# Revit family: LAMP_FIL 70 OPAL SUSPENDED DALI
name_source: partatom
category: Luminarias
revit_build: Autodesk Revit 2015 (Build: 20140606_1530(x64)
units: mm (PartAtom-declared; Revit-internal decimal feet)

## types (16) — shared parameters
CRI = 80
Cambio de temperatura de color de luz atenuada = <Ninguno>
Comentarios de tipo = Availability of switching between accessories through visibility parameters when placed in a project.
Fabricante = LAMP
Filtro de color = 16777215
Gear = Adjustable DALI
IEE = A+
IFC Clasificación = Light Fixture
Installation instructions = https://www.lamp.es
Insulation class = I
Last update = 12/08/2020
Luminaire type = Indoor - Modular System
Lámpara = LED MID-POWER
MacAdam = 3
Manufacturer URL = http://www.lamp.es
Manufacturer country = Spain
Manufacturer name = LAMP
Material Difusor = LAMP_PC Difusor Opal Fil
Model explanation = Availability of switching between accessories through visibility parameters when placed in a project.
Power Supply = 220-240V 50-60Hz
Product URL = https://www.lamp.es
Product datasheet = https://www.lamp.es
Protection rating = IP42, IK06
Type = MID POWER PHILIPS
Ángulo de inclinación = 90,00°

## per-type parameters (varying)
| type | Archivo de red fotométrica | Descripción | Dimensiones | Efficacy | Finish | LED Lifetime | Largo | Longitud de línea de emisión | Material Perfil | Material codo | Modelo | Plum | Power | Product code | UniClass 1.4 Code | UniClass 2.0 Code | Weight |
| 1162MM 2600LM 3000K GREY | 4741483.IES | FIL 70 OPAL SUS 2600 WW DALI GR. | 1.162x70x70mm | 104 lm/W | Gloss Grey | 60000 L80 B10 | 1162 mm  [stored 3.81234 ft] | 1162 mm  [stored 3.81234 ft] | LAMP_Aluminio Perfil Fil GR | LAMP_Aluminio Perfil Fil GR | F71SF120LOOP830DG | 19 W | 17 W | F71SF120LOOP830DG | F71SF120LOOP830DG | F71SF120LOOP830DG | 2,54 kg |
| 1162MM 2600LM 3000K WHITE | 4741480.IES | FIL 70 OPAL SUS 2600 WW DALI WH. | 1.162x70x70mm | 104 lm/W | Matt White | 60000 L80 B10 | 1162 mm  [stored 3.81234 ft] | 1162 mm  [stored 3.81234 ft] | LAMP_Aluminio Perfil Fil BL | LAMP_Aluminio Perfil Fil BL | F71SF120LOOP830DW | 19 W | 17 W | F71SF120LOOP830DW | F71SF120LOOP830DW | F71SF120LOOP830DW | 2,54 kg |
| 1162MM 2600LM 4000K GREY | 4740483.IES | FIL 70 OPAL SUS 2600 NW DALI GR. | 1.162x70x70mm | 112 lm/W | Gloss Grey | 60000 L80 B10 | 1162 mm  [stored 3.81234 ft] | 1162 mm  [stored 3.81234 ft] | LAMP_Aluminio Perfil Fil GR | LAMP_Aluminio Perfil Fil GR | F71SF120LOOP840DG | 19 W | 17 W | F71SF120LOOP840DG | F71SF120LOOP840DG | F71SF120LOOP840DG | 2,54 kg |
| 1162MM 2600LM 4000K WHITE | 4740480.IES | FIL 70 OPAL SUS 2600 NW DALI WH. | 1.162x70x70mm | 112 lm/W | Matt White | 60000 L80 B10 | 1162 mm  [stored 3.81234 ft] | 1162 mm  [stored 3.81234 ft] | LAMP_Aluminio Perfil Fil BL | LAMP_Aluminio Perfil Fil BL | F71SF120LOOP840DW | 19 W | 17 W | F71SF120LOOP840DW | F71SF120LOOP840DW | F71SF120LOOP840DW | 2,54 kg |
| 1162MM 4400LM 3000K GREY | 4741563.IES | FIL 70 OPAL SUS 4400 WW DALI GR. | 1.162x70x70mm | 110 lm/W | Gloss Grey | 60000 L80 B10 | 1162 mm  [stored 3.81234 ft] | 1162 mm  [stored 3.81234 ft] | LAMP_Aluminio Perfil Fil GR | LAMP_Aluminio Perfil Fil GR | F71SF120HOOP830DG | 31 W | 28 W | F71SF120HOOP830DG | F71SF120HOOP830DG | F71SF120HOOP830DG | 2,53 kg |
| 1162MM 4400LM 3000K WHITE | 4741560.IES | FIL 70 OPAL SUS 4400 WW DALI WH. | 1.162x70x70mm | 110 lm/W | Matt White | 60000 L80 B10 | 1162 mm  [stored 3.81234 ft] | 1162 mm  [stored 3.81234 ft] | LAMP_Aluminio Perfil Fil BL | LAMP_Aluminio Perfil Fil BL | F71SF120HOOP830DW | 31 W | 28 W | F71SF120HOOP830DW | F71SF120HOOP830DW | F71SF120HOOP830DW | 2,53 kg |
| 1162MM 4400LM 4000K GREY | 4740563.IES | FIL 70 OPAL SUS 4400 NW DALI GR. | 1.162x70x70mm | 116 lm/W | Gloss Grey | 60000 L80 B10 | 1162 mm  [stored 3.81234 ft] | 1162 mm  [stored 3.81234 ft] | LAMP_Aluminio Perfil Fil GR | LAMP_Aluminio Perfil Fil GR | F71SF120HOOP840DG | 31 W | 28 W | F71SF120HOOP840DG | F71SF120HOOP840DG | F71SF120HOOP840DG | 2,53 kg |
| 1162MM 4400LM 4000K WHITE | 4740560.IES | FIL 70 OPAL SUS 4400 NW DALI WH. | 1.162x70x70mm | 116 lm/W | Gloss Grey | 60000 L80 B10 | 1162 mm  [stored 3.81234 ft] | 1162 mm  [stored 3.81234 ft] | LAMP_Aluminio Perfil Fil BL | LAMP_Aluminio Perfil Fil BL | F71SF120HOOP840DW | 31 W | 28 W | F71SF120HOOP840DW | F71SF120HOOP840DW | F71SF120HOOP840DW | 2,53 kg |
| 1743MM 3900LM 3000K GREY | 4741493.IES | FIL 70 OPAL SUS 3900 WW DALI GR. | 1.743x70x70mm | 101 lm/W | Gloss Grey | 50000 L80 B10 | 1743 mm  [stored 5.7185 ft] | 1743 mm  [stored 5.7185 ft] | LAMP_Aluminio Perfil Fil GR | LAMP_Aluminio Perfil Fil GR | F71SF170LOOP830DG | 30 W | 25 W | F71SF170LOOP830DG | F71SF170LOOP830DG | F71SF170LOOP830DG | 4,09 kg |
| 1743MM 3900LM 3000K WHITE | 4741490.IES | FIL 70 OPAL SUS 3900 WW DALI WH. | 1.743x70x70mm | 101 lm/W | Matt White | 50000 L80 B10 | 1743 mm  [stored 5.7185 ft] | 1743 mm  [stored 5.7185 ft] | LAMP_Aluminio Perfil Fil BL | LAMP_Aluminio Perfil Fil BL | F71SF170LOOP830DW | 30 W | 25 W | F71SF170LOOP830DW | F71SF170LOOP830DW | F71SF170LOOP830DW | 4,09 kg |
| 1743MM 3900LM 4000K GREY | 4740493.IES | FIL 70 OPAL SUS 3900 NW DALI GR. | 1.743x70x70mm | 108 lm/W | Gloss Grey | 50000 L80 B10 | 1743 mm  [stored 5.7185 ft] | 1743 mm  [stored 5.7185 ft] | LAMP_Aluminio Perfil Fil GR | LAMP_Aluminio Perfil Fil GR | F71SF170LOOP840DG | 30 W | 25 W | F71SF170LOOP840DG | F71SF170LOOP840DG | F71SF170LOOP840DG | 4,09 kg |
| 1743MM 3900LM 4000K WHITE | 4740490.IES | FIL 70 OPAL SUS 3900 NW DALI WH. | 1.743x70x70mm | 108 lm/W | Matt White | 50000 L80 B10 | 1743 mm  [stored 5.7185 ft] | 1743 mm  [stored 5.7185 ft] | LAMP_Aluminio Perfil Fil BL | LAMP_Aluminio Perfil Fil BL | F71SF170LOOP840DW | 30 W | 25 W | F71SF170LOOP840DW | F71SF170LOOP840DW | F71SF170LOOP840DW | 4,09 kg |
| 1743MM 6600LM 3000K GREY | 4741573.IES | FIL 70 OPAL SUS 6600 WW DALI GR. | 1.743x70x70mm | 110 lm/W | Gloss Grey | 50000 L80 B10 | 1743 mm  [stored 5.7185 ft] | 1743 mm  [stored 5.7185 ft] | LAMP_Aluminio Perfil Fil GR | LAMP_Aluminio Perfil Fil GR | F71SF170HOOP830DG | 46 W | 41 W | F71SF170HOOP830DG | F71SF170HOOP830DG | F71SF170HOOP830DG | 4,09 kg |
| 1743MM 6600LM 3000K WHITE | 4741570.IES | FIL 70 OPAL SUS 6600 WW DALI WH. | 1.743x70x70mm | 110 lm/W | Matt White | 50000 L80 B10 | 1743 mm  [stored 5.7185 ft] | 1743 mm  [stored 5.7185 ft] | LAMP_Aluminio Perfil Fil BL | LAMP_Aluminio Perfil Fil BL | F71SF170HOOP830DW | 46 W | 41 W | F71SF170HOOP830DW | F71SF170HOOP830DW | F71SF170HOOP830DW | 4,09 kg |
| 1743MM 6600LM 4000K GREY | 4740573.IES | FIL 70 OPAL SUS 6600 NW DALI GR. | 1.743x70x70mm | 116 lm/W | Gloss Grey | 50000 L80 B10 | 1743 mm  [stored 5.7185 ft] | 1743 mm  [stored 5.7185 ft] | LAMP_Aluminio Perfil Fil GR | LAMP_Aluminio Perfil Fil GR | F71SF170HOOP840DG | 46 W | 41 W | F71SF170HOOP840DG | F71SF170HOOP840DG | F71SF170HOOP840DG | 4,09 kg |
| 1743MM 6600LM 4000K WHITE | 4740570.IES | FIL 70 OPAL SUS 6600 NW DALI WH. | 1.743x70x70mm | 116 lm/W | Matt White | 50000 L80 B10 | 1743 mm  [stored 5.7185 ft] | 1743 mm  [stored 5.7185 ft] | LAMP_Aluminio Perfil Fil BL | LAMP_Aluminio Perfil Fil BL | F71SF170HOOP840DW | 46 W | 41 W | F71SF170HOOP840DW | F71SF170HOOP840DW | F71SF170HOOP840DW | 4,09 kg |

note: [stored X ft] marks values corroborated as IEEE doubles in the binary element streams (Revit-internal decimal feet)

## geometry (parser evidence)
native form markers: Blend x5
no freeform markers — native parametric forms only
